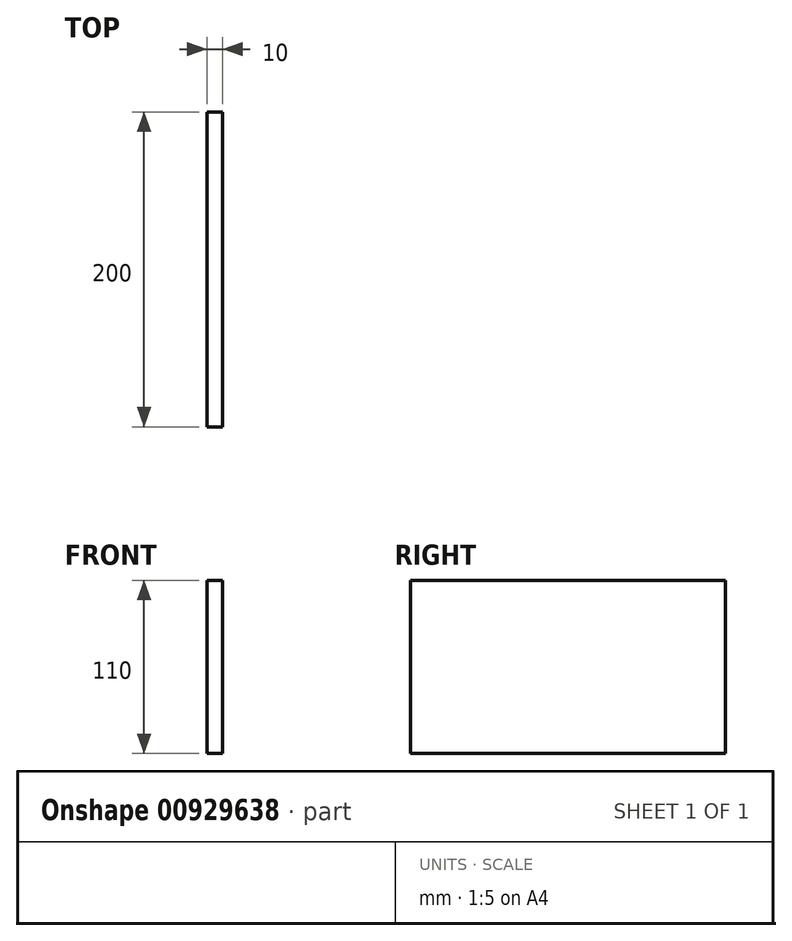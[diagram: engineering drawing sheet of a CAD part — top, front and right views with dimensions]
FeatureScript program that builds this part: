
annotation { "Feature Type Name" : "Feature", "Feature Type Description" : "" }
export const myFeature = defineFeature(function(context is Context, id is Id, definition is map)
    precondition{}
    {
        {
            var Q0;
            Q0=qCreatedBy(makeId("Right.planeOp"),FACE);
            var sketch = newSketch(context, id + "F0", { "sketchPlane" : qUnion([Q0])});
            skLineSegment(sketch, "E0.bottom", {"start": v(0, 0) * mm, "end": v(200, 0) * mm});
            skLineSegment(sketch, "E0.top", {"start": v(0, 110) * mm, "end": v(200, 110) * mm});
            skLineSegment(sketch, "E0.left", {"start": v(0, 0) * mm, "end": v(0, 110) * mm});
            skLineSegment(sketch, "E0.right", {"start": v(200, 0) * mm, "end": v(200, 110) * mm});
            skSolve(sketch);
        }
        {
            var Q0;
            Q0=makeQuery(id+"F0.imprint","IMPRINT",FACE,{"disambiguationData":[TD([[makeQuery(id+"F0.imprint","IMPRINT",EDGE,{"derivedFrom":sQuery(id+"F0.wireOp",EDGE,"E0.bottom")}),1.0]])]});
            extrude(context, id + "F1", {"entities" : qUnion([Q0]), "depth" : 10 * mm, "offsetDistance" : 25 * mm});
        }
    });
